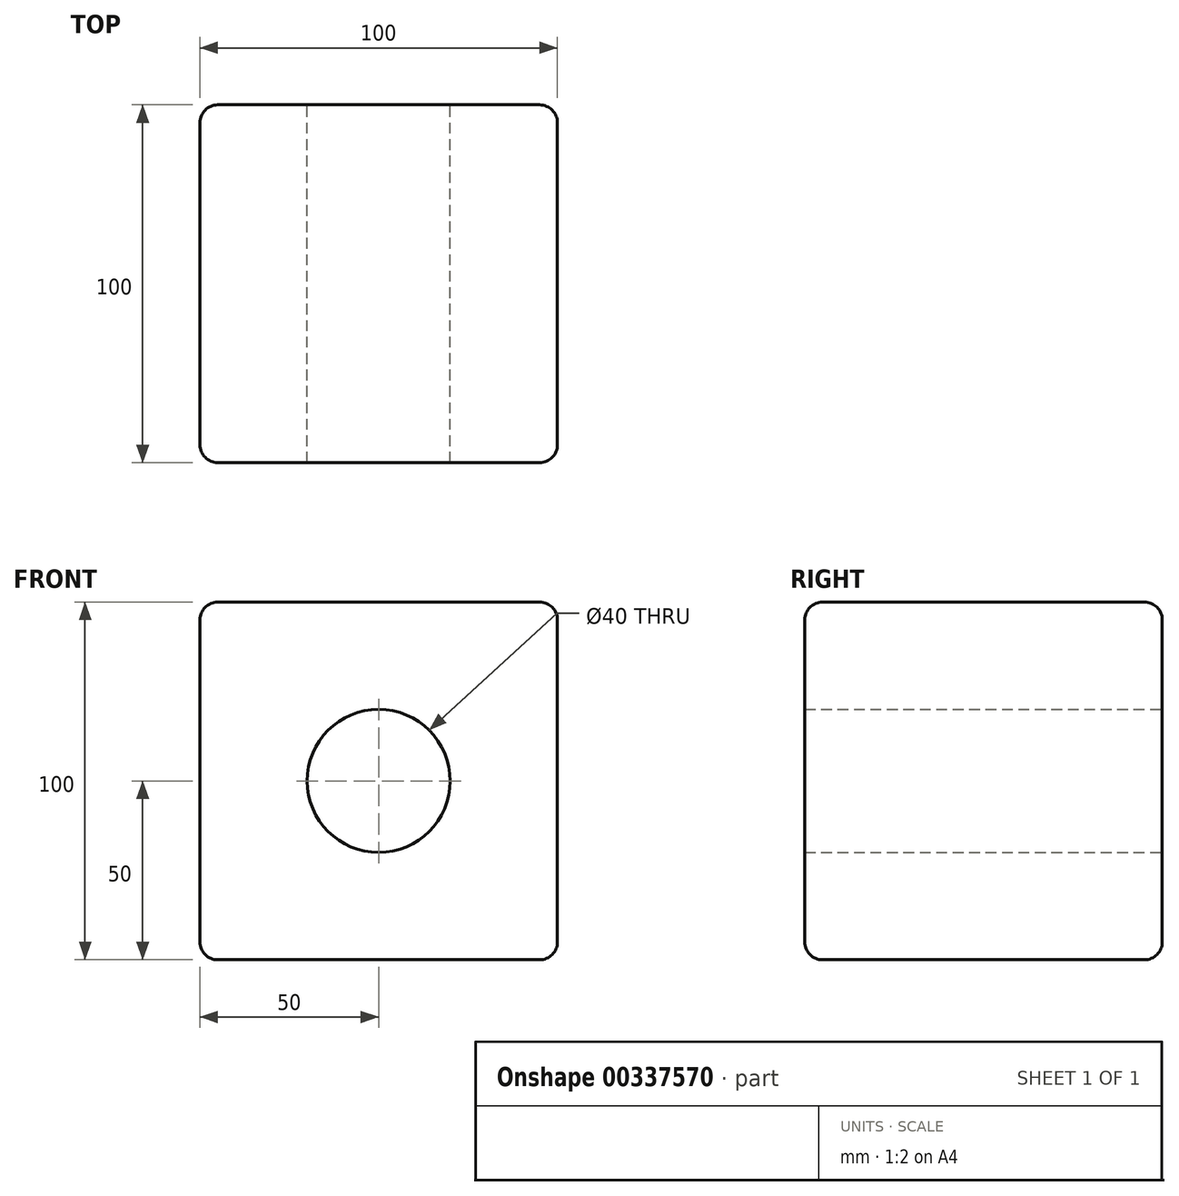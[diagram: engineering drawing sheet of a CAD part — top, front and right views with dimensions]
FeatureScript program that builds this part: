
annotation { "Feature Type Name" : "Feature", "Feature Type Description" : "" }
export const myFeature = defineFeature(function(context is Context, id is Id, definition is map)
    precondition{}
    {
        {
            var Q0;
            Q0=qCreatedBy(makeId("Front.planeOp"),FACE);
            var sketch = newSketch(context, id + "F0", { "sketchPlane" : qUnion([Q0])});
            skLineSegment(sketch, "E0.bottom", {"start": v(0, 0) * mm, "end": v(100, 0) * mm});
            skLineSegment(sketch, "E0.top", {"start": v(0, 100) * mm, "end": v(100, 100) * mm});
            skLineSegment(sketch, "E0.left", {"start": v(0, 0) * mm, "end": v(0, 100) * mm});
            skLineSegment(sketch, "E0.right", {"start": v(100, 0) * mm, "end": v(100, 100) * mm});
            skSolve(sketch);
        }
        {
            var Q0;
            Q0 = qSketchRegion(id + "F0", true);
            extrude(context, id + "F1", {"entities" : qUnion([Q0]), "depth" : 100 * mm});
        }
        {
            var Q0;
            Q0=makeQuery(id+"F1.opExtrude","CAP_EDGE",EDGE,{"disambiguationData":[OSD([sQuery(id+"F0.wireOp",EDGE,"E0.top")])],"isStart":false});
            var Q1;
            Q1=makeQuery(id+"F1.opExtrude","CAP_EDGE",EDGE,{"disambiguationData":[OSD([sQuery(id+"F0.wireOp",EDGE,"E0.bottom")])],"isStart":false});
            var Q2;
            Q2=makeQuery(id+"F1.opExtrude","SWEPT_EDGE",EDGE,{"disambiguationData":[OSD([sQuery(id+"F0.wireOp",EDGE,"E0.bottom"),sQuery(id+"F0.wireOp",EDGE,"E0.left")])]});
            var Q3;
            Q3=makeQuery(id+"F1.opExtrude","CAP_EDGE",EDGE,{"disambiguationData":[OSD([sQuery(id+"F0.wireOp",EDGE,"E0.left")])],"isStart":false});
            var Q4;
            Q4=makeQuery(id+"F1.opExtrude","SWEPT_EDGE",EDGE,{"disambiguationData":[OSD([sQuery(id+"F0.wireOp",EDGE,"E0.top"),sQuery(id+"F0.wireOp",EDGE,"E0.left")])]});
            var Q5;
            Q5=makeQuery(id+"F1.opExtrude","SWEPT_EDGE",EDGE,{"disambiguationData":[OSD([sQuery(id+"F0.wireOp",EDGE,"E0.top"),sQuery(id+"F0.wireOp",EDGE,"E0.right")])]});
            var Q6;
            Q6=makeQuery(id+"F1.opExtrude","CAP_EDGE",EDGE,{"disambiguationData":[OSD([sQuery(id+"F0.wireOp",EDGE,"E0.top")])],"isStart":true});
            var Q7;
            Q7=makeQuery(id+"F1.opExtrude","CAP_EDGE",EDGE,{"disambiguationData":[OSD([sQuery(id+"F0.wireOp",EDGE,"E0.left")])],"isStart":true});
            var Q8;
            Q8=makeQuery(id+"F1.opExtrude","CAP_EDGE",EDGE,{"disambiguationData":[OSD([sQuery(id+"F0.wireOp",EDGE,"E0.bottom")])],"isStart":true});
            var Q9;
            Q9=makeQuery(id+"F1.opExtrude","CAP_EDGE",EDGE,{"disambiguationData":[OSD([sQuery(id+"F0.wireOp",EDGE,"E0.right")])],"isStart":true});
            var Q10;
            Q10=makeQuery(id+"F1.opExtrude","SWEPT_EDGE",EDGE,{"disambiguationData":[OSD([sQuery(id+"F0.wireOp",EDGE,"E0.bottom"),sQuery(id+"F0.wireOp",EDGE,"E0.right")])]});
            var Q11;
            Q11=makeQuery(id+"F1.opExtrude","CAP_EDGE",EDGE,{"disambiguationData":[OSD([sQuery(id+"F0.wireOp",EDGE,"E0.right")])],"isStart":false});
            fillet(context, id + "F2", {"entities" : qUnion([Q0, Q1, Q2, Q3, Q4, Q5, Q6, Q7, Q8, Q9, Q10, Q11]), "radius" : 5 * mm, "tangentPropagation" : true, "allowEdgeOverflow" : false});
        }
        {
            var Q0;
            Q0=makeQuery(id+"F1.opExtrude","CAP_FACE",FACE,{"disambiguationData":[OSD([sQuery(id+"F0.wireOp",EDGE,"E0.bottom"),sQuery(id+"F0.wireOp",EDGE,"E0.top"),sQuery(id+"F0.wireOp",EDGE,"E0.left"),sQuery(id+"F0.wireOp",EDGE,"E0.right")])],"isStart":true});
            var sketch = newSketch(context, id + "F3", { "sketchPlane" : qUnion([Q0])});
            skLineSegment(sketch, "E1", {"start": v(-95, 50) * mm, "end": v(-5, 50) * mm, "construction": true});
            skCircle(sketch, "E2", {"center": v(-50, 50) * mm, "radius": 20 * mm});
            skSolve(sketch);
        }
        {
            var Q0;
            Q0 = qSketchRegion(id + "F3", true);
            extrude(context, id + "F4", {"entities" : qUnion([Q0]), "operationType" : NewBodyOperationType.REMOVE, "oppositeDirection" : true, "depth" : 100 * mm});
        }
    });
